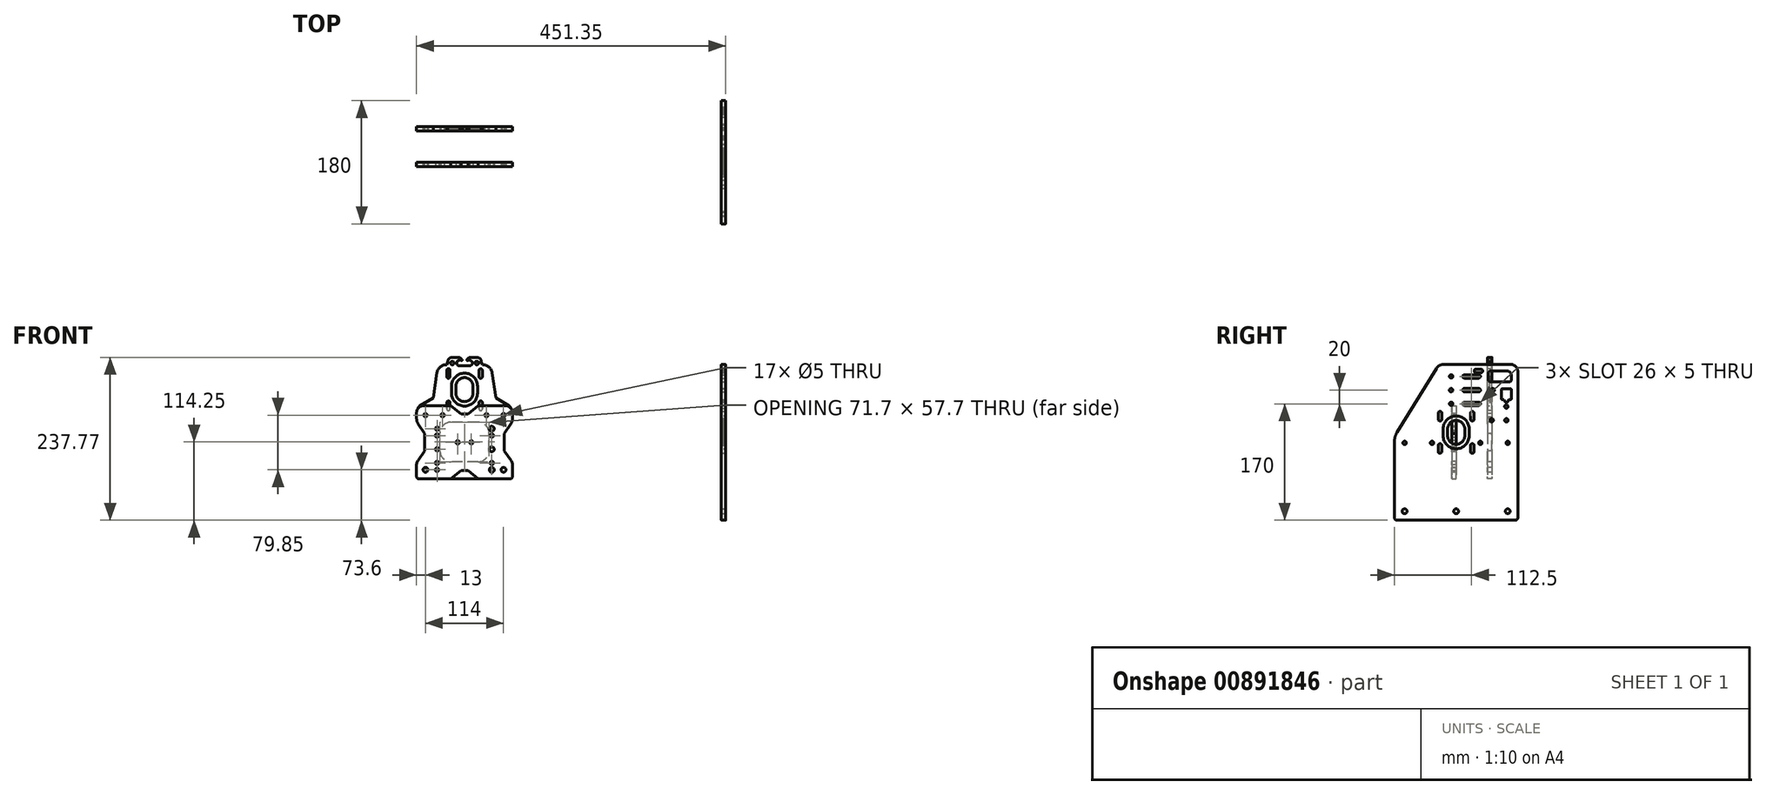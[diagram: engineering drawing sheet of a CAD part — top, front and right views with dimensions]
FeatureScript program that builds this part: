
annotation { "Feature Type Name" : "Feature", "Feature Type Description" : "" }
export const myFeature = defineFeature(function(context is Context, id is Id, definition is map)
    precondition{}
    {
        {
            var Q0;
            Q0=qCreatedBy(makeId("Right.planeOp"),FACE);
            var sketch = newSketch(context, id + "F0", { "sketchPlane" : qUnion([Q0])});
            skLineSegment(sketch, "E0", {"start": v(-28.77, 108.05) * mm, "end": v(-86.28, 14.78) * mm});
            skLineSegment(sketch, "E1", {"start": v(-90, 1.66) * mm, "end": v(-90, -110.25) * mm});
            skLineSegment(sketch, "E2", {"start": v(-86.5, -113.75) * mm, "end": v(86.5, -113.75) * mm});
            skLineSegment(sketch, "E3", {"start": v(90, -110.25) * mm, "end": v(90, 103.75) * mm});
            skLineSegment(sketch, "E4", {"start": v(80, 113.75) * mm, "end": v(-18.55, 113.75) * mm});
            skLineSegment(sketch, "E5", {"start": v(0, -113.75) * mm, "end": v(0, 0) * mm, "construction": true});
            skLineSegment(sketch, "E6", {"start": v(0, 0) * mm, "end": v(0, 113.75) * mm, "construction": true});
            skPoint(sketch, "E7.visualSharp", {"position": v(-25.25, 113.75) * mm});
            skArc(sketch, "E7.filletArc", {"start": v(-18.55, 113.75) * mm, "mid": v(-24.4, 112.23) * mm, "end": v(-28.77, 108.05) * mm});
            skPoint(sketch, "E8.visualSharp", {"position": v(90, 113.75) * mm});
            skArc(sketch, "E8.filletArc", {"start": v(90, 103.75) * mm, "mid": v(87.07, 110.82) * mm, "end": v(80, 113.75) * mm});
            skPoint(sketch, "E9.visualSharp", {"position": v(-90, -113.75) * mm});
            skArc(sketch, "E9.filletArc", {"start": v(-90, -110.25) * mm, "mid": v(-88.97, -112.72) * mm, "end": v(-86.5, -113.75) * mm});
            skPoint(sketch, "E10.visualSharp", {"position": v(90, -113.75) * mm});
            skArc(sketch, "E10.filletArc", {"start": v(86.5, -113.75) * mm, "mid": v(88.97, -112.72) * mm, "end": v(90, -110.25) * mm});
            skPoint(sketch, "E11.visualSharp", {"position": v(-90, 8.75) * mm});
            skArc(sketch, "E11.filletArc", {"start": v(-86.28, 14.78) * mm, "mid": v(-89.05, 8.48) * mm, "end": v(-90, 1.66) * mm});
            skSolve(sketch);
        }
        {
            var Q0;
            Q0=qSketchRegion(id+"F0",true);
            extrude(context, id + "F1", {"entities" : qUnion([Q0]), "depth" : 6.35 * mm});
        }
        {
            var Q0;
            Q0=makeQuery(id+"F1.opExtrude","CAP_FACE",FACE,{"disambiguationData":[OSD([sQuery(id+"F0.wireOp",EDGE,"E0"),sQuery(id+"F0.wireOp",EDGE,"E1"),sQuery(id+"F0.wireOp",EDGE,"E2"),sQuery(id+"F0.wireOp",EDGE,"E3"),sQuery(id+"F0.wireOp",EDGE,"E4"),sQuery(id+"F0.wireOp",EDGE,"E7.filletArc"),sQuery(id+"F0.wireOp",EDGE,"E8.filletArc"),sQuery(id+"F0.wireOp",EDGE,"E9.filletArc"),sQuery(id+"F0.wireOp",EDGE,"E10.filletArc"),sQuery(id+"F0.wireOp",EDGE,"E11.filletArc")])],"isStart":false});
            var sketch = newSketch(context, id + "F2", { "sketchPlane" : qUnion([Q0])});
            skLineSegment(sketch, "E12", {"start": v(0, 0) * mm, "end": v(0, -100.75) * mm, "construction": true});
            skLineSegment(sketch, "E13", {"start": v(0, -100.75) * mm, "end": v(75.3, -100.75) * mm, "construction": true});
            skLineSegment(sketch, "E14", {"start": v(0, -100.75) * mm, "end": v(-75.3, -100.75) * mm, "construction": true});
            skCircle(sketch, "E15", {"center": v(-75.3, -100.75) * mm, "radius": 3.57 * mm});
            skCircle(sketch, "E16", {"center": v(75.3, -100.75) * mm, "radius": 3.57 * mm});
            skCircle(sketch, "E17", {"center": v(0, -100.75) * mm, "radius": 3.57 * mm});
            skLineSegment(sketch, "E18", {"start": v(-75.3, -0.75) * mm, "end": v(-35.3, -0.75) * mm, "construction": true});
            skLineSegment(sketch, "E19", {"start": v(-35.3, -0.75) * mm, "end": v(0, -0.75) * mm, "construction": true});
            skLineSegment(sketch, "E20", {"start": v(0, -0.75) * mm, "end": v(35.3, -0.75) * mm, "construction": true});
            skLineSegment(sketch, "E21", {"start": v(35.3, -0.75) * mm, "end": v(75.3, -0.75) * mm, "construction": true});
            skCircle(sketch, "E22", {"center": v(-75.3, -0.75) * mm, "radius": 2.5 * mm});
            skCircle(sketch, "E23", {"center": v(-35.3, -0.75) * mm, "radius": 2.5 * mm});
            skCircle(sketch, "E24", {"center": v(35.3, -0.75) * mm, "radius": 2.5 * mm});
            skCircle(sketch, "E25", {"center": v(75.3, -0.75) * mm, "radius": 2.5 * mm});
            skLineSegment(sketch, "E26", {"start": v(-75.3, -0.75) * mm, "end": v(-75.3, -100.75) * mm, "construction": true});
            skLineSegment(sketch, "E27", {"start": v(75.3, -0.75) * mm, "end": v(75.3, -100.75) * mm, "construction": true});
            skSolve(sketch);
        }
        {
            var Q0;
            Q0=qSketchRegion(id+"F2",true);
            extrude(context, id + "F3", {"entities" : qUnion([Q0]), "operationType" : NewBodyOperationType.REMOVE, "endBound" : BoundingType.THROUGH_ALL, "oppositeDirection" : true, "depth" : 25 * mm});
        }
        {
            var Q0;
            Q0=makeQuery(id+"F1.opExtrude","CAP_FACE",FACE,{"disambiguationData":[OSD([sQuery(id+"F0.wireOp",EDGE,"E0"),sQuery(id+"F0.wireOp",EDGE,"E1"),sQuery(id+"F0.wireOp",EDGE,"E2"),sQuery(id+"F0.wireOp",EDGE,"E3"),sQuery(id+"F0.wireOp",EDGE,"E4"),sQuery(id+"F0.wireOp",EDGE,"E7.filletArc"),sQuery(id+"F0.wireOp",EDGE,"E8.filletArc"),sQuery(id+"F0.wireOp",EDGE,"E9.filletArc"),sQuery(id+"F0.wireOp",EDGE,"E10.filletArc"),sQuery(id+"F0.wireOp",EDGE,"E11.filletArc")])],"isStart":false});
            var sketch = newSketch(context, id + "F4", { "sketchPlane" : qUnion([Q0])});
            skArc(sketch, "E28", {"start": v(-12.5, 9.55) * mm, "mid": v(0, -2.95) * mm, "end": v(12.5, 9.55) * mm});
            skLineSegment(sketch, "E29", {"start": v(-12.5, 9.55) * mm, "end": v(-12.5, 19.55) * mm});
            skLineSegment(sketch, "E30", {"start": v(12.5, 19.55) * mm, "end": v(12.5, 9.55) * mm});
            skArc(sketch, "E31", {"start": v(-12.5, 19.55) * mm, "mid": v(0, 32.05) * mm, "end": v(12.5, 19.55) * mm});
            skLineSegment(sketch, "E32", {"start": v(0, 19.55) * mm, "end": v(0, 9.55) * mm, "construction": true});
            skLineSegment(sketch, "E33", {"start": v(-35.3, -0.75) * mm, "end": v(35.3, -0.75) * mm, "construction": true});
            skLineSegment(sketch, "E34", {"start": v(-23.57, 42.62) * mm, "end": v(-23.57, 33.62) * mm, "construction": true});
            skArc(sketch, "E35", {"start": v(-21.02, 42.62) * mm, "mid": v(-23.57, 45.17) * mm, "end": v(-26.12, 42.62) * mm});
            skArc(sketch, "E36", {"start": v(-26.12, 33.62) * mm, "mid": v(-23.57, 31.07) * mm, "end": v(-21.02, 33.62) * mm});
            skLineSegment(sketch, "E37", {"start": v(-21.02, 42.62) * mm, "end": v(-21.02, 33.62) * mm});
            skLineSegment(sketch, "E38", {"start": v(-26.12, 33.62) * mm, "end": v(-26.12, 42.62) * mm});
            skLineSegment(sketch, "E39", {"start": v(-12.5, 14.55) * mm, "end": v(12.5, 14.55) * mm, "construction": true});
            skLineSegment(sketch, "E40.MirrorCS", {"start": v(23.57, 42.62) * mm, "end": v(23.57, 33.62) * mm, "construction": true});
            skArc(sketch, "E41.MirrorCS", {"start": v(26.12, 33.62) * mm, "mid": v(23.57, 31.07) * mm, "end": v(21.02, 33.62) * mm});
            skLineSegment(sketch, "E42.MirrorCS", {"start": v(21.02, 42.62) * mm, "end": v(21.02, 33.62) * mm});
            skArc(sketch, "E43.MirrorCS", {"start": v(21.02, 42.62) * mm, "mid": v(23.57, 45.17) * mm, "end": v(26.12, 42.62) * mm});
            skLineSegment(sketch, "E44.MirrorCS", {"start": v(26.12, 33.62) * mm, "end": v(26.12, 42.62) * mm});
            skArc(sketch, "E45.MirrorCS", {"start": v(26.12, -4.52) * mm, "mid": v(23.57, -1.97) * mm, "end": v(21.02, -4.52) * mm});
            skLineSegment(sketch, "E46.MirrorCS", {"start": v(26.12, -4.52) * mm, "end": v(26.12, -13.52) * mm});
            skLineSegment(sketch, "E47.MirrorCS", {"start": v(-23.57, -13.52) * mm, "end": v(-23.57, -4.52) * mm, "construction": true});
            skLineSegment(sketch, "E48.MirrorCS", {"start": v(23.57, -13.52) * mm, "end": v(23.57, -4.52) * mm, "construction": true});
            skArc(sketch, "E49.MirrorCS", {"start": v(21.02, -13.52) * mm, "mid": v(23.57, -16.07) * mm, "end": v(26.12, -13.52) * mm});
            skLineSegment(sketch, "E50.MirrorCS", {"start": v(21.02, -13.52) * mm, "end": v(21.02, -4.52) * mm});
            skArc(sketch, "E51.MirrorCS", {"start": v(-26.12, -4.52) * mm, "mid": v(-23.57, -1.97) * mm, "end": v(-21.02, -4.52) * mm});
            skLineSegment(sketch, "E52.MirrorCS", {"start": v(-21.02, -13.52) * mm, "end": v(-21.02, -4.52) * mm});
            skArc(sketch, "E53.MirrorCS", {"start": v(-21.02, -13.52) * mm, "mid": v(-23.57, -16.07) * mm, "end": v(-26.12, -13.52) * mm});
            skLineSegment(sketch, "E54.MirrorCS", {"start": v(-26.12, -4.52) * mm, "end": v(-26.12, -13.52) * mm});
            skLineSegment(sketch, "E55", {"start": v(-23.57, 38.12) * mm, "end": v(23.57, -9.02) * mm, "construction": true});
            skLineSegment(sketch, "E56", {"start": v(23.57, -9.02) * mm, "end": v(-23.57, -9.02) * mm, "construction": true});
            skLineSegment(sketch, "E57", {"start": v(-23.57, -9.02) * mm, "end": v(23.57, 38.12) * mm, "construction": true});
            skSolve(sketch);
        }
        {
            var Q0;
            Q0=qSketchRegion(id+"F4",true);
            extrude(context, id + "F5", {"entities" : qUnion([Q0]), "operationType" : NewBodyOperationType.REMOVE, "endBound" : BoundingType.THROUGH_ALL, "oppositeDirection" : true, "depth" : 25 * mm});
        }
        {
            var Q0;
            Q0=makeQuery(id+"F1.opExtrude","CAP_FACE",FACE,{"disambiguationData":[OSD([sQuery(id+"F0.wireOp",EDGE,"E0"),sQuery(id+"F0.wireOp",EDGE,"E1"),sQuery(id+"F0.wireOp",EDGE,"E2"),sQuery(id+"F0.wireOp",EDGE,"E3"),sQuery(id+"F0.wireOp",EDGE,"E4"),sQuery(id+"F0.wireOp",EDGE,"E7.filletArc"),sQuery(id+"F0.wireOp",EDGE,"E8.filletArc"),sQuery(id+"F0.wireOp",EDGE,"E9.filletArc"),sQuery(id+"F0.wireOp",EDGE,"E10.filletArc"),sQuery(id+"F0.wireOp",EDGE,"E11.filletArc")])],"isStart":false});
            var sketch = newSketch(context, id + "F6", { "sketchPlane" : qUnion([Q0])});
            skCircle(sketch, "E58", {"center": v(-7.35, 96.25) * mm, "radius": 2.5 * mm});
            skLineSegment(sketch, "E59", {"start": v(-7.35, 96.25) * mm, "end": v(12, 96.25) * mm, "construction": true});
            skLineSegment(sketch, "E60", {"start": v(12, 96.25) * mm, "end": v(33, 96.25) * mm, "construction": true});
            skArc(sketch, "E61", {"start": v(12, 93.75) * mm, "mid": v(9.5, 96.25) * mm, "end": v(12, 98.75) * mm});
            skArc(sketch, "E62", {"start": v(33, 98.75) * mm, "mid": v(35.5, 96.25) * mm, "end": v(33, 93.75) * mm});
            skLineSegment(sketch, "E63", {"start": v(12, 98.75) * mm, "end": v(33, 98.75) * mm});
            skLineSegment(sketch, "E64", {"start": v(12, 93.75) * mm, "end": v(33, 93.75) * mm});
            skCircle(sketch, "E65.0.1.0", {"center": v(-7.35, 76.25) * mm, "radius": 2.5 * mm});
            skLineSegment(sketch, "E65.0.1.1", {"start": v(-7.35, 76.25) * mm, "end": v(12, 76.25) * mm, "construction": true});
            skArc(sketch, "E65.0.1.2", {"start": v(12, 73.75) * mm, "mid": v(9.5, 76.25) * mm, "end": v(12, 78.75) * mm});
            skLineSegment(sketch, "E65.0.1.3", {"start": v(12, 78.75) * mm, "end": v(33, 78.75) * mm});
            skLineSegment(sketch, "E65.0.1.4", {"start": v(12, 73.75) * mm, "end": v(33, 73.75) * mm});
            skArc(sketch, "E65.0.1.5", {"start": v(33, 78.75) * mm, "mid": v(35.5, 76.25) * mm, "end": v(33, 73.75) * mm});
            skCircle(sketch, "E65.0.2.0", {"center": v(-7.35, 56.25) * mm, "radius": 2.5 * mm});
            skLineSegment(sketch, "E65.0.2.1", {"start": v(-7.35, 56.25) * mm, "end": v(12, 56.25) * mm, "construction": true});
            skArc(sketch, "E65.0.2.2", {"start": v(12, 53.75) * mm, "mid": v(9.5, 56.25) * mm, "end": v(12, 58.75) * mm});
            skLineSegment(sketch, "E65.0.2.3", {"start": v(12, 58.75) * mm, "end": v(33, 58.75) * mm});
            skLineSegment(sketch, "E65.0.2.4", {"start": v(12, 53.75) * mm, "end": v(33, 53.75) * mm});
            skArc(sketch, "E65.0.2.5", {"start": v(33, 58.75) * mm, "mid": v(35.5, 56.25) * mm, "end": v(33, 53.75) * mm});
            skLineSegment(sketch, "E65.direction1", {"start": v(-7.35, 96.25) * mm, "end": v(-7.35, 96.25) * mm});
            skLineSegment(sketch, "E65.direction2", {"start": v(-7.35, 96.25) * mm, "end": v(-7.35, 76.25) * mm, "construction": true});
            skLineSegment(sketch, "E66", {"start": v(33, 76.25) * mm, "end": v(12, 76.25) * mm, "construction": true});
            skLineSegment(sketch, "E67", {"start": v(12, 56.25) * mm, "end": v(33, 56.25) * mm, "construction": true});
            skLineSegment(sketch, "E68", {"start": v(33, 76.25) * mm, "end": v(53.35, 76.25) * mm, "construction": true});
            skPoint(sketch, "E68.endSnap0", {"position": v(35.5, 76.25) * mm});
            skCircle(sketch, "E69", {"center": v(53.35, 76.25) * mm, "radius": 2.5 * mm});
            skSolve(sketch);
        }
        {
            var Q0;
            Q0=qSketchRegion(id+"F6",true);
            extrude(context, id + "F7", {"entities" : qUnion([Q0]), "operationType" : NewBodyOperationType.REMOVE, "endBound" : BoundingType.THROUGH_ALL, "oppositeDirection" : true, "depth" : 25 * mm});
        }
        {
            var Q0;
            Q0=makeQuery(id+"F1.opExtrude","CAP_FACE",FACE,{"disambiguationData":[OSD([sQuery(id+"F0.wireOp",EDGE,"E0"),sQuery(id+"F0.wireOp",EDGE,"E1"),sQuery(id+"F0.wireOp",EDGE,"E2"),sQuery(id+"F0.wireOp",EDGE,"E3"),sQuery(id+"F0.wireOp",EDGE,"E4"),sQuery(id+"F0.wireOp",EDGE,"E7.filletArc"),sQuery(id+"F0.wireOp",EDGE,"E8.filletArc"),sQuery(id+"F0.wireOp",EDGE,"E9.filletArc"),sQuery(id+"F0.wireOp",EDGE,"E10.filletArc"),sQuery(id+"F0.wireOp",EDGE,"E11.filletArc")])],"isStart":false});
            var sketch = newSketch(context, id + "F8", { "sketchPlane" : qUnion([Q0])});
            skLineSegment(sketch, "E70", {"start": v(12, 96.25) * mm, "end": v(33, 96.25) * mm, "construction": true});
            skLineSegment(sketch, "E71.bottom", {"start": v(28.1, 106.75) * mm, "end": v(36.9, 106.75) * mm});
            skLineSegment(sketch, "E71.top", {"start": v(28.1, 101.75) * mm, "end": v(36.9, 101.75) * mm});
            skLineSegment(sketch, "E71.left", {"start": v(26.5, 105.15) * mm, "end": v(26.5, 103.35) * mm});
            skLineSegment(sketch, "E71.right", {"start": v(38.5, 105.15) * mm, "end": v(38.5, 103.35) * mm});
            skPoint(sketch, "E72.visualSharp", {"position": v(26.5, 101.75) * mm});
            skArc(sketch, "E72.filletArc", {"start": v(26.5, 103.35) * mm, "mid": v(26.97, 102.22) * mm, "end": v(28.1, 101.75) * mm});
            skPoint(sketch, "E73.visualSharp", {"position": v(26.5, 106.75) * mm});
            skArc(sketch, "E73.filletArc", {"start": v(28.1, 106.75) * mm, "mid": v(26.97, 106.28) * mm, "end": v(26.5, 105.15) * mm});
            skPoint(sketch, "E74.visualSharp", {"position": v(38.5, 106.75) * mm});
            skArc(sketch, "E74.filletArc", {"start": v(38.5, 105.15) * mm, "mid": v(38.03, 106.28) * mm, "end": v(36.9, 106.75) * mm});
            skPoint(sketch, "E75.visualSharp", {"position": v(38.5, 101.75) * mm});
            skArc(sketch, "E75.filletArc", {"start": v(36.9, 101.75) * mm, "mid": v(38.03, 102.22) * mm, "end": v(38.5, 103.35) * mm});
            skLineSegment(sketch, "E76", {"start": v(26.5, 104.25) * mm, "end": v(38.5, 104.25) * mm, "construction": true});
            skLineSegment(sketch, "E77", {"start": v(32.5, 106.75) * mm, "end": v(32.5, 101.75) * mm, "construction": true});
            skLineSegment(sketch, "E78", {"start": v(22.5, 96.25) * mm, "end": v(22.5, 56.25) * mm, "construction": true});
            skPoint(sketch, "E78.endSnap0", {"position": v(22.5, 58.75) * mm});
            skLineSegment(sketch, "E79", {"start": v(12, 56.25) * mm, "end": v(33, 56.25) * mm, "construction": true});
            skSolve(sketch);
        }
        {
            var Q0;
            Q0=qSketchRegion(id+"F8",true);
            extrude(context, id + "F9", {"entities" : qUnion([Q0]), "operationType" : NewBodyOperationType.REMOVE, "endBound" : BoundingType.THROUGH_ALL, "oppositeDirection" : true, "depth" : 25 * mm});
        }
        {
            var Q0;
            Q0=makeQuery(id+"F1.opExtrude","CAP_FACE",FACE,{"disambiguationData":[OSD([sQuery(id+"F0.wireOp",EDGE,"E0"),sQuery(id+"F0.wireOp",EDGE,"E1"),sQuery(id+"F0.wireOp",EDGE,"E2"),sQuery(id+"F0.wireOp",EDGE,"E3"),sQuery(id+"F0.wireOp",EDGE,"E4"),sQuery(id+"F0.wireOp",EDGE,"E7.filletArc"),sQuery(id+"F0.wireOp",EDGE,"E8.filletArc"),sQuery(id+"F0.wireOp",EDGE,"E9.filletArc"),sQuery(id+"F0.wireOp",EDGE,"E10.filletArc"),sQuery(id+"F0.wireOp",EDGE,"E11.filletArc")])],"isStart":false});
            var sketch = newSketch(context, id + "F10", { "sketchPlane" : qUnion([Q0])});
            skCircle(sketch, "E80", {"center": v(73.3, 52.25) * mm, "radius": 2.5 * mm});
            skLineSegment(sketch, "E81", {"start": v(73.3, 52.25) * mm, "end": v(73.3, 32.25) * mm, "construction": true});
            skCircle(sketch, "E82", {"center": v(73.3, 32.25) * mm, "radius": 2.5 * mm});
            skLineSegment(sketch, "E83", {"start": v(73.3, 32.25) * mm, "end": v(51.95, 32.25) * mm, "construction": true});
            skCircle(sketch, "E84", {"center": v(51.95, 32.25) * mm, "radius": 2.5 * mm});
            skLineSegment(sketch, "E85", {"start": v(12, 56.25) * mm, "end": v(33, 56.25) * mm, "construction": true});
            skLineSegment(sketch, "E86", {"start": v(33, 56.25) * mm, "end": v(33, 52.25) * mm, "construction": true});
            skLineSegment(sketch, "E87", {"start": v(33, 52.25) * mm, "end": v(73.3, 52.25) * mm, "construction": true});
            skSolve(sketch);
        }
        {
            var Q0;
            Q0=qSketchRegion(id+"F10",true);
            extrude(context, id + "F11", {"entities" : qUnion([Q0]), "operationType" : NewBodyOperationType.REMOVE, "endBound" : BoundingType.THROUGH_ALL, "oppositeDirection" : true, "depth" : 25 * mm});
        }
        {
            var Q0;
            Q0=makeQuery(id+"F1.opExtrude","CAP_FACE",FACE,{"disambiguationData":[OSD([sQuery(id+"F0.wireOp",EDGE,"E0"),sQuery(id+"F0.wireOp",EDGE,"E1"),sQuery(id+"F0.wireOp",EDGE,"E2"),sQuery(id+"F0.wireOp",EDGE,"E3"),sQuery(id+"F0.wireOp",EDGE,"E4"),sQuery(id+"F0.wireOp",EDGE,"E7.filletArc"),sQuery(id+"F0.wireOp",EDGE,"E8.filletArc"),sQuery(id+"F0.wireOp",EDGE,"E9.filletArc"),sQuery(id+"F0.wireOp",EDGE,"E10.filletArc"),sQuery(id+"F0.wireOp",EDGE,"E11.filletArc")])],"isStart":false});
            var sketch = newSketch(context, id + "F12", { "sketchPlane" : qUnion([Q0])});
            skLineSegment(sketch, "E88", {"start": v(65.95, 76.8) * mm, "end": v(65.95, 63.85) * mm});
            skLineSegment(sketch, "E89", {"start": v(67.55, 62.25) * mm, "end": v(69.65, 62.25) * mm});
            skLineSegment(sketch, "E90", {"start": v(69.65, 62.25) * mm, "end": v(70.8, 60.75) * mm});
            skLineSegment(sketch, "E91", {"start": v(75.8, 60.75) * mm, "end": v(76.95, 62.25) * mm});
            skLineSegment(sketch, "E92", {"start": v(76.95, 62.25) * mm, "end": v(79.05, 62.25) * mm});
            skLineSegment(sketch, "E93", {"start": v(80.65, 63.85) * mm, "end": v(80.65, 76.8) * mm});
            skLineSegment(sketch, "E94", {"start": v(79.05, 78.4) * mm, "end": v(67.55, 78.4) * mm});
            skArc(sketch, "E95", {"start": v(70.8, 60.75) * mm, "mid": v(73.3, 58.25) * mm, "end": v(75.8, 60.75) * mm});
            skLineSegment(sketch, "E96", {"start": v(73.3, 60.75) * mm, "end": v(73.3, 52.25) * mm, "construction": true});
            skLineSegment(sketch, "E97", {"start": v(73.3, 78.4) * mm, "end": v(73.3, 60.75) * mm, "construction": true});
            skLineSegment(sketch, "E98", {"start": v(65.95, 70.32) * mm, "end": v(80.65, 70.32) * mm, "construction": true});
            skPoint(sketch, "E99.visualSharp", {"position": v(65.95, 62.25) * mm});
            skArc(sketch, "E99.filletArc", {"start": v(65.95, 63.85) * mm, "mid": v(66.42, 62.72) * mm, "end": v(67.55, 62.25) * mm});
            skPoint(sketch, "E100.visualSharp", {"position": v(65.95, 78.4) * mm});
            skArc(sketch, "E100.filletArc", {"start": v(67.55, 78.4) * mm, "mid": v(66.42, 77.93) * mm, "end": v(65.95, 76.8) * mm});
            skPoint(sketch, "E101.visualSharp", {"position": v(80.65, 78.4) * mm});
            skArc(sketch, "E101.filletArc", {"start": v(80.65, 76.8) * mm, "mid": v(80.18, 77.93) * mm, "end": v(79.05, 78.4) * mm});
            skPoint(sketch, "E102.visualSharp", {"position": v(80.65, 62.25) * mm});
            skArc(sketch, "E102.filletArc", {"start": v(79.05, 62.25) * mm, "mid": v(80.18, 62.72) * mm, "end": v(80.65, 63.85) * mm});
            skLineSegment(sketch, "E103", {"start": v(80.65, 91.4) * mm, "end": v(80.65, 97.6) * mm});
            skLineSegment(sketch, "E104", {"start": v(74, 104.25) * mm, "end": v(50.3, 104.25) * mm});
            skLineSegment(sketch, "E105", {"start": v(47.15, 101.1) * mm, "end": v(47.15, 91.4) * mm});
            skLineSegment(sketch, "E106", {"start": v(50.3, 88.25) * mm, "end": v(77.5, 88.25) * mm});
            skPoint(sketch, "E107.visualSharp", {"position": v(80.65, 104.25) * mm});
            skArc(sketch, "E107.filletArc", {"start": v(80.65, 97.6) * mm, "mid": v(78.7, 102.3) * mm, "end": v(74, 104.25) * mm});
            skPoint(sketch, "E108.visualSharp", {"position": v(80.65, 88.25) * mm});
            skArc(sketch, "E108.filletArc", {"start": v(77.5, 88.25) * mm, "mid": v(79.73, 89.17) * mm, "end": v(80.65, 91.4) * mm});
            skPoint(sketch, "E109.visualSharp", {"position": v(47.15, 88.25) * mm});
            skArc(sketch, "E109.filletArc", {"start": v(47.15, 91.4) * mm, "mid": v(48.07, 89.17) * mm, "end": v(50.3, 88.25) * mm});
            skPoint(sketch, "E110.visualSharp", {"position": v(47.15, 104.25) * mm});
            skArc(sketch, "E110.filletArc", {"start": v(50.3, 104.25) * mm, "mid": v(48.07, 103.33) * mm, "end": v(47.15, 101.1) * mm});
            skSolve(sketch);
        }
        {
            var Q0;
            Q0=qSketchRegion(id+"F12",true);
            extrude(context, id + "F13", {"entities" : qUnion([Q0]), "operationType" : NewBodyOperationType.REMOVE, "endBound" : BoundingType.THROUGH_ALL, "oppositeDirection" : true, "depth" : 25 * mm});
        }
        {
            var Q0;
            Q0=makeQuery(id+"F1.opExtrude","SWEPT_BODY",BODY,{"disambiguationData":[OSD([sQuery(id+"F0.wireOp",EDGE,"E0"),sQuery(id+"F0.wireOp",EDGE,"E1"),sQuery(id+"F0.wireOp",EDGE,"E2"),sQuery(id+"F0.wireOp",EDGE,"E3"),sQuery(id+"F0.wireOp",EDGE,"E4"),sQuery(id+"F0.wireOp",EDGE,"E7.filletArc"),sQuery(id+"F0.wireOp",EDGE,"E8.filletArc"),sQuery(id+"F0.wireOp",EDGE,"E9.filletArc"),sQuery(id+"F0.wireOp",EDGE,"E10.filletArc"),sQuery(id+"F0.wireOp",EDGE,"E11.filletArc")])]});
            transform(context, id + "F14", {"entities" : qUnion([Q0]), "transformType" : TransformType.TRANSLATION_3D, "dx" : (750 / 2) * mm, "dy" : 0 * mm, "dz" : 0 * mm, "makeCopy" : false});
        }
        {
            var Q0;
            Q0=qCreatedBy(makeId("Front.planeOp"),FACE);
            var sketch = newSketch(context, id + "F15", { "sketchPlane" : qUnion([Q0])});
            skLineSegment(sketch, "E111", {"start": v(0, 0) * mm, "end": v(0, 41.2) * mm, "construction": true});
            skLineSegment(sketch, "E112", {"start": v(0, 0) * mm, "end": v(0, -41.2) * mm, "construction": true});
            skLineSegment(sketch, "E113", {"start": v(0, 41.2) * mm, "end": v(5, 41.2) * mm});
            skLineSegment(sketch, "E114", {"start": v(20, 53.35) * mm, "end": v(5, 41.2) * mm});
            skLineSegment(sketch, "E115", {"start": v(20, 53.35) * mm, "end": v(70, 53.35) * mm});
            skLineSegment(sketch, "E116", {"start": v(70, 53.35) * mm, "end": v(70, 30.5) * mm});
            skLineSegment(sketch, "E117", {"start": v(70, 30.5) * mm, "end": v(58, 12.75) * mm});
            skLineSegment(sketch, "E118", {"start": v(58, 12.75) * mm, "end": v(58, -12.75) * mm});
            skLineSegment(sketch, "E119", {"start": v(58, -12.75) * mm, "end": v(70, -29.25) * mm});
            skLineSegment(sketch, "E120", {"start": v(70, -29.25) * mm, "end": v(70, -53.35) * mm});
            skLineSegment(sketch, "E121", {"start": v(70, -53.35) * mm, "end": v(20, -53.35) * mm});
            skLineSegment(sketch, "E122", {"start": v(20, -53.35) * mm, "end": v(5, -41.2) * mm});
            skLineSegment(sketch, "E123", {"start": v(5, -41.2) * mm, "end": v(0, -41.2) * mm});
            skLineSegment(sketch, "E124", {"start": v(20, 53.35) * mm, "end": v(20, -53.35) * mm, "construction": true});
            skLineSegment(sketch, "E125", {"start": v(0, 41.2) * mm, "end": v(0, 53.35) * mm, "construction": true});
            skLineSegment(sketch, "E126", {"start": v(0, 53.35) * mm, "end": v(20, 53.35) * mm, "construction": true});
            skLineSegment(sketch, "E127", {"start": v(0, -41.2) * mm, "end": v(0, -53.35) * mm, "construction": true});
            skLineSegment(sketch, "E128", {"start": v(0, -53.35) * mm, "end": v(20, -53.35) * mm, "construction": true});
            skLineSegment(sketch, "E129", {"start": v(5, 41.2) * mm, "end": v(5, -41.2) * mm, "construction": true});
            skLineSegment(sketch, "E130", {"start": v(0, 0) * mm, "end": v(58, 0) * mm, "construction": true});
            skLineSegment(sketch, "E131", {"start": v(70, 30.5) * mm, "end": v(70, -29.25) * mm, "construction": true});
            skLineSegment(sketch, "E132.MirrorCS", {"start": v(-5, -41.2) * mm, "end": v(0, -41.2) * mm});
            skLineSegment(sketch, "E133.MirrorCS", {"start": v(-20, -53.35) * mm, "end": v(-5, -41.2) * mm});
            skLineSegment(sketch, "E134.MirrorCS", {"start": v(-70, -53.35) * mm, "end": v(-20, -53.35) * mm});
            skLineSegment(sketch, "E135.MirrorCS", {"start": v(-70, -29.25) * mm, "end": v(-70, -53.35) * mm});
            skLineSegment(sketch, "E136.MirrorCS", {"start": v(-58, -12.75) * mm, "end": v(-70, -29.25) * mm});
            skLineSegment(sketch, "E137.MirrorCS", {"start": v(-58, 12.75) * mm, "end": v(-58, -12.75) * mm});
            skLineSegment(sketch, "E138.MirrorCS", {"start": v(-70, 30.5) * mm, "end": v(-58, 12.75) * mm});
            skLineSegment(sketch, "E139.MirrorCS", {"start": v(-70, 53.35) * mm, "end": v(-70, 30.5) * mm});
            skLineSegment(sketch, "E140.MirrorCS", {"start": v(-20, 53.35) * mm, "end": v(-70, 53.35) * mm});
            skLineSegment(sketch, "E141.MirrorCS", {"start": v(0, 41.2) * mm, "end": v(-5, 41.2) * mm});
            skLineSegment(sketch, "E142.MirrorCS", {"start": v(-20, 53.35) * mm, "end": v(-5, 41.2) * mm});
            skSolve(sketch);
        }
        {
            var Q0;
            Q0=qSketchRegion(id+"F15",true);
            extrude(context, id + "F16", {"entities" : qUnion([Q0]), "depth" : 6.35 * mm});
        }
        {
            var Q0;
            Q0=makeQuery(id+"F16.opExtrude","CAP_FACE",FACE,{"disambiguationData":[OSD([sQuery(id+"F15.wireOp",EDGE,"E113"),sQuery(id+"F15.wireOp",EDGE,"E114"),sQuery(id+"F15.wireOp",EDGE,"E115"),sQuery(id+"F15.wireOp",EDGE,"E116"),sQuery(id+"F15.wireOp",EDGE,"E117"),sQuery(id+"F15.wireOp",EDGE,"E118"),sQuery(id+"F15.wireOp",EDGE,"E119"),sQuery(id+"F15.wireOp",EDGE,"E120"),sQuery(id+"F15.wireOp",EDGE,"E121"),sQuery(id+"F15.wireOp",EDGE,"E122"),sQuery(id+"F15.wireOp",EDGE,"E123"),sQuery(id+"F15.wireOp",EDGE,"E132.MirrorCS"),sQuery(id+"F15.wireOp",EDGE,"E133.MirrorCS"),sQuery(id+"F15.wireOp",EDGE,"E134.MirrorCS"),sQuery(id+"F15.wireOp",EDGE,"E135.MirrorCS"),sQuery(id+"F15.wireOp",EDGE,"E136.MirrorCS"),sQuery(id+"F15.wireOp",EDGE,"E137.MirrorCS"),sQuery(id+"F15.wireOp",EDGE,"E138.MirrorCS"),sQuery(id+"F15.wireOp",EDGE,"E139.MirrorCS"),sQuery(id+"F15.wireOp",EDGE,"E140.MirrorCS"),sQuery(id+"F15.wireOp",EDGE,"E141.MirrorCS"),sQuery(id+"F15.wireOp",EDGE,"E142.MirrorCS")])],"isStart":false});
            var sketch = newSketch(context, id + "F17", { "sketchPlane" : qUnion([Q0])});
            skLineSegment(sketch, "E143", {"start": v(0, 0) * mm, "end": v(10, 0) * mm, "construction": true});
            skLineSegment(sketch, "E144", {"start": v(0, 0) * mm, "end": v(-10, 0) * mm, "construction": true});
            skCircle(sketch, "E145", {"center": v(-10, 0) * mm, "radius": 2.5 * mm});
            skCircle(sketch, "E146", {"center": v(10, 0) * mm, "radius": 2.5 * mm});
            skSolve(sketch);
        }
        {
            var Q0;
            Q0=qSketchRegion(id+"F17",true);
            extrude(context, id + "F18", {"entities" : qUnion([Q0]), "operationType" : NewBodyOperationType.REMOVE, "endBound" : BoundingType.THROUGH_ALL, "oppositeDirection" : true, "depth" : 25 * mm});
        }
        {
            var Q0;
            Q0=makeQuery(id+"F16.opExtrude","CAP_FACE",FACE,{"disambiguationData":[OSD([sQuery(id+"F15.wireOp",EDGE,"E113"),sQuery(id+"F15.wireOp",EDGE,"E114"),sQuery(id+"F15.wireOp",EDGE,"E115"),sQuery(id+"F15.wireOp",EDGE,"E116"),sQuery(id+"F15.wireOp",EDGE,"E117"),sQuery(id+"F15.wireOp",EDGE,"E118"),sQuery(id+"F15.wireOp",EDGE,"E119"),sQuery(id+"F15.wireOp",EDGE,"E120"),sQuery(id+"F15.wireOp",EDGE,"E121"),sQuery(id+"F15.wireOp",EDGE,"E122"),sQuery(id+"F15.wireOp",EDGE,"E123"),sQuery(id+"F15.wireOp",EDGE,"E132.MirrorCS"),sQuery(id+"F15.wireOp",EDGE,"E133.MirrorCS"),sQuery(id+"F15.wireOp",EDGE,"E134.MirrorCS"),sQuery(id+"F15.wireOp",EDGE,"E135.MirrorCS"),sQuery(id+"F15.wireOp",EDGE,"E136.MirrorCS"),sQuery(id+"F15.wireOp",EDGE,"E137.MirrorCS"),sQuery(id+"F15.wireOp",EDGE,"E138.MirrorCS"),sQuery(id+"F15.wireOp",EDGE,"E139.MirrorCS"),sQuery(id+"F15.wireOp",EDGE,"E140.MirrorCS"),sQuery(id+"F15.wireOp",EDGE,"E141.MirrorCS"),sQuery(id+"F15.wireOp",EDGE,"E142.MirrorCS")])],"isStart":false});
            var sketch = newSketch(context, id + "F19", { "sketchPlane" : qUnion([Q0])});
            skLineSegment(sketch, "E147", {"start": v(0, 41.2) * mm, "end": v(0, -41.2) * mm, "construction": true});
            skLineSegment(sketch, "E148", {"start": v(32, 39.7) * mm, "end": v(57, 39.7) * mm, "construction": true});
            skCircle(sketch, "E149", {"center": v(32, 39.7) * mm, "radius": 2.5 * mm});
            skCircle(sketch, "E150", {"center": v(57, 39.7) * mm, "radius": 2.5 * mm});
            skCircle(sketch, "E151", {"center": v(57, -40.1) * mm, "radius": 3.57 * mm});
            skCircle(sketch, "E152.MirrorC", {"center": v(-57, -40.1) * mm, "radius": 3.57 * mm});
            skCircle(sketch, "E153.MirrorC", {"center": v(-57, 39.7) * mm, "radius": 2.5 * mm});
            skCircle(sketch, "E154.MirrorC", {"center": v(-32, 39.7) * mm, "radius": 2.5 * mm});
            skLineSegment(sketch, "E155", {"start": v(-57, 39.7) * mm, "end": v(-32, 39.7) * mm, "construction": true});
            skLineSegment(sketch, "E156", {"start": v(57, 39.7) * mm, "end": v(57, -40.1) * mm, "construction": true});
            skLineSegment(sketch, "E157", {"start": v(-57, 39.7) * mm, "end": v(-57, -40.1) * mm, "construction": true});
            skLineSegment(sketch, "E158", {"start": v(-57, -40.1) * mm, "end": v(57, -40.1) * mm, "construction": true});
            skLineSegment(sketch, "E159", {"start": v(-32, 39.7) * mm, "end": v(32, 39.7) * mm, "construction": true});
            skSolve(sketch);
        }
        {
            var Q0;
            Q0=qSketchRegion(id+"F19",true);
            extrude(context, id + "F20", {"entities" : qUnion([Q0]), "operationType" : NewBodyOperationType.REMOVE, "endBound" : BoundingType.THROUGH_ALL, "oppositeDirection" : true, "depth" : 25 * mm});
        }
        {
            var Q0;
            Q0=makeQuery(id+"F16.opExtrude","CAP_FACE",FACE,{"disambiguationData":[OSD([sQuery(id+"F15.wireOp",EDGE,"E113"),sQuery(id+"F15.wireOp",EDGE,"E114"),sQuery(id+"F15.wireOp",EDGE,"E115"),sQuery(id+"F15.wireOp",EDGE,"E116"),sQuery(id+"F15.wireOp",EDGE,"E117"),sQuery(id+"F15.wireOp",EDGE,"E118"),sQuery(id+"F15.wireOp",EDGE,"E119"),sQuery(id+"F15.wireOp",EDGE,"E120"),sQuery(id+"F15.wireOp",EDGE,"E121"),sQuery(id+"F15.wireOp",EDGE,"E122"),sQuery(id+"F15.wireOp",EDGE,"E123"),sQuery(id+"F15.wireOp",EDGE,"E132.MirrorCS"),sQuery(id+"F15.wireOp",EDGE,"E133.MirrorCS"),sQuery(id+"F15.wireOp",EDGE,"E134.MirrorCS"),sQuery(id+"F15.wireOp",EDGE,"E135.MirrorCS"),sQuery(id+"F15.wireOp",EDGE,"E136.MirrorCS"),sQuery(id+"F15.wireOp",EDGE,"E137.MirrorCS"),sQuery(id+"F15.wireOp",EDGE,"E138.MirrorCS"),sQuery(id+"F15.wireOp",EDGE,"E139.MirrorCS"),sQuery(id+"F15.wireOp",EDGE,"E140.MirrorCS"),sQuery(id+"F15.wireOp",EDGE,"E141.MirrorCS"),sQuery(id+"F15.wireOp",EDGE,"E142.MirrorCS")])],"isStart":false});
            var sketch = newSketch(context, id + "F21", { "sketchPlane" : qUnion([Q0])});
            skLineSegment(sketch, "E160", {"start": v(0, 41.2) * mm, "end": v(0, -41.2) * mm, "construction": true});
            skLineSegment(sketch, "E161", {"start": v(39.8, 9.85) * mm, "end": v(39.8, -10.15) * mm, "construction": true});
            skLineSegment(sketch, "E162", {"start": v(39.8, -10.15) * mm, "end": v(39.8, -30.15) * mm, "construction": true});
            skLineSegment(sketch, "E163", {"start": v(39.8, 9.85) * mm, "end": v(39.8, 19.85) * mm, "construction": true});
            skLineSegment(sketch, "E164", {"start": v(39.8, -30.15) * mm, "end": v(39.8, -40.15) * mm, "construction": true});
            skCircle(sketch, "E165", {"center": v(39.8, 19.85) * mm, "radius": 3.57 * mm});
            skCircle(sketch, "E166", {"center": v(39.8, -10.15) * mm, "radius": 3.57 * mm});
            skCircle(sketch, "E167", {"center": v(39.8, -40.15) * mm, "radius": 3.57 * mm});
            skCircle(sketch, "E168", {"center": v(39.8, 9.85) * mm, "radius": 2.5 * mm});
            skCircle(sketch, "E169", {"center": v(39.8, -30.15) * mm, "radius": 2.5 * mm});
            skLineSegment(sketch, "E170", {"start": v(39.8, -10.15) * mm, "end": v(0, -10.15) * mm, "construction": true});
            skLineSegment(sketch, "E171", {"start": v(-40, 9.85) * mm, "end": v(-40, 19.85) * mm, "construction": true});
            skLineSegment(sketch, "E172", {"start": v(-40, -30.15) * mm, "end": v(-40, -40.15) * mm, "construction": true});
            skCircle(sketch, "E173", {"center": v(-40, 19.85) * mm, "radius": 2.5 * mm});
            skCircle(sketch, "E174", {"center": v(-40, 9.85) * mm, "radius": 2.5 * mm});
            skCircle(sketch, "E175", {"center": v(-40, -10.15) * mm, "radius": 2.5 * mm});
            skCircle(sketch, "E176", {"center": v(-40, -30.15) * mm, "radius": 2.5 * mm});
            skCircle(sketch, "E177", {"center": v(-40, -40.15) * mm, "radius": 2.5 * mm});
            skLineSegment(sketch, "E178", {"start": v(-40, -30.15) * mm, "end": v(-40, -10.15) * mm, "construction": true});
            skLineSegment(sketch, "E179", {"start": v(-40, 9.85) * mm, "end": v(-40, -10.15) * mm, "construction": true});
            skLineSegment(sketch, "E180", {"start": v(-40, -10.15) * mm, "end": v(0, -10.15) * mm, "construction": true});
            skSolve(sketch);
        }
        {
            var Q0;
            Q0=qSketchRegion(id+"F21",true);
            extrude(context, id + "F22", {"entities" : qUnion([Q0]), "operationType" : NewBodyOperationType.REMOVE, "endBound" : BoundingType.THROUGH_ALL, "oppositeDirection" : true, "depth" : 25 * mm});
        }
        {
            var Q0;
            Q0=makeQuery(id+"F16.opExtrude","SWEPT_EDGE",EDGE,{"disambiguationData":[OSD([sQuery(id+"F15.wireOp",EDGE,"E139.MirrorCS"),sQuery(id+"F15.wireOp",EDGE,"E140.MirrorCS")])]});
            var Q1;
            Q1=makeQuery(id+"F16.opExtrude","SWEPT_EDGE",EDGE,{"disambiguationData":[OSD([sQuery(id+"F15.wireOp",EDGE,"E115"),sQuery(id+"F15.wireOp",EDGE,"E116")])]});
            fillet(context, id + "F23", {"entities" : qUnion([Q0, Q1]), "radius" : 9.6 * mm, "tangentPropagation" : true, "allowEdgeOverflow" : false});
        }
        {
            var Q0;
            Q0=makeQuery(id+"F16.opExtrude","SWEPT_EDGE",EDGE,{"disambiguationData":[OSD([sQuery(id+"F15.wireOp",EDGE,"E120"),sQuery(id+"F15.wireOp",EDGE,"E121")])]});
            var Q1;
            Q1=makeQuery(id+"F16.opExtrude","SWEPT_EDGE",EDGE,{"disambiguationData":[OSD([sQuery(id+"F15.wireOp",EDGE,"E134.MirrorCS"),sQuery(id+"F15.wireOp",EDGE,"E135.MirrorCS")])]});
            fillet(context, id + "F24", {"entities" : qUnion([Q0, Q1]), "radius" : 3.36 * mm, "tangentPropagation" : true, "allowEdgeOverflow" : false});
        }
        {
            var Q0;
            Q0=makeQuery(id+"F16.opExtrude","SWEPT_EDGE",EDGE,{"disambiguationData":[OSD([sQuery(id+"F15.wireOp",EDGE,"E116"),sQuery(id+"F15.wireOp",EDGE,"E117")])]});
            var Q1;
            Q1=makeQuery(id+"F16.opExtrude","SWEPT_EDGE",EDGE,{"disambiguationData":[OSD([sQuery(id+"F15.wireOp",EDGE,"E138.MirrorCS"),sQuery(id+"F15.wireOp",EDGE,"E139.MirrorCS")])]});
            fillet(context, id + "F25", {"entities" : qUnion([Q0, Q1]), "radius" : 14 * mm, "tangentPropagation" : true, "allowEdgeOverflow" : false});
        }
        {
            var Q0;
            Q0=makeQuery(id+"F16.opExtrude","SWEPT_EDGE",EDGE,{"disambiguationData":[OSD([sQuery(id+"F15.wireOp",EDGE,"E119"),sQuery(id+"F15.wireOp",EDGE,"E120")])]});
            var Q1;
            Q1=makeQuery(id+"F16.opExtrude","SWEPT_EDGE",EDGE,{"disambiguationData":[OSD([sQuery(id+"F15.wireOp",EDGE,"E135.MirrorCS"),sQuery(id+"F15.wireOp",EDGE,"E136.MirrorCS")])]});
            fillet(context, id + "F26", {"entities" : qUnion([Q0, Q1]), "radius" : 11 * mm, "tangentPropagation" : true, "allowEdgeOverflow" : false});
        }
        {
            var Q0;
            Q0=makeQuery(id+"F16.opExtrude","CAP_FACE",FACE,{"disambiguationData":[OSD([sQuery(id+"F15.wireOp",EDGE,"E113"),sQuery(id+"F15.wireOp",EDGE,"E114"),sQuery(id+"F15.wireOp",EDGE,"E115"),sQuery(id+"F15.wireOp",EDGE,"E116"),sQuery(id+"F15.wireOp",EDGE,"E117"),sQuery(id+"F15.wireOp",EDGE,"E118"),sQuery(id+"F15.wireOp",EDGE,"E119"),sQuery(id+"F15.wireOp",EDGE,"E120"),sQuery(id+"F15.wireOp",EDGE,"E121"),sQuery(id+"F15.wireOp",EDGE,"E122"),sQuery(id+"F15.wireOp",EDGE,"E123"),sQuery(id+"F15.wireOp",EDGE,"E132.MirrorCS"),sQuery(id+"F15.wireOp",EDGE,"E133.MirrorCS"),sQuery(id+"F15.wireOp",EDGE,"E134.MirrorCS"),sQuery(id+"F15.wireOp",EDGE,"E135.MirrorCS"),sQuery(id+"F15.wireOp",EDGE,"E136.MirrorCS"),sQuery(id+"F15.wireOp",EDGE,"E137.MirrorCS"),sQuery(id+"F15.wireOp",EDGE,"E138.MirrorCS"),sQuery(id+"F15.wireOp",EDGE,"E139.MirrorCS"),sQuery(id+"F15.wireOp",EDGE,"E140.MirrorCS"),sQuery(id+"F15.wireOp",EDGE,"E141.MirrorCS"),sQuery(id+"F15.wireOp",EDGE,"E142.MirrorCS")])],"isStart":true});
            cPlane(context, id + "F27", {"entities" : qUnion([Q0]), "cplaneType" : CPlaneType.OFFSET, "offset" : 46 * mm, "width" : 150 * mm, "height" : 150 * mm});
        }
        {
            var Q0;
            Q0=qCreatedBy(id+"F27.planeOp",FACE);
            var sketch = newSketch(context, id + "F28", { "sketchPlane" : qUnion([Q0])});
            skLineSegment(sketch, "E181", {"start": v(0, 0) * mm, "end": v(0, -53.35) * mm, "construction": true});
            skLineSegment(sketch, "E182", {"start": v(-67.5, 51.95) * mm, "end": v(-45.84, 64.81) * mm});
            skLineSegment(sketch, "E183", {"start": v(-45.84, 64.81) * mm, "end": v(-38.5, 113.35) * mm});
            skLineSegment(sketch, "E184", {"start": v(-38.5, 113.35) * mm, "end": v(-26, 113.35) * mm});
            skLineSegment(sketch, "E185", {"start": v(-26, 113.35) * mm, "end": v(-22.45, 124.02) * mm, "construction": true});
            skLineSegment(sketch, "E186", {"start": v(-22.45, 124.02) * mm, "end": v(0, 124.02) * mm, "construction": true});
            skLineSegment(sketch, "E187", {"start": v(0, 124.02) * mm, "end": v(0, 0) * mm, "construction": true});
            skLineSegment(sketch, "E188.MirrorCS", {"start": v(22.45, 124.02) * mm, "end": v(0, 124.02) * mm, "construction": true});
            skLineSegment(sketch, "E189.MirrorCS", {"start": v(26, 113.35) * mm, "end": v(22.45, 124.02) * mm, "construction": true});
            skLineSegment(sketch, "E190.MirrorCS", {"start": v(38.5, 113.35) * mm, "end": v(26, 113.35) * mm});
            skLineSegment(sketch, "E191.MirrorCS", {"start": v(45.84, 64.81) * mm, "end": v(38.5, 113.35) * mm});
            skLineSegment(sketch, "E192.MirrorCS", {"start": v(67.5, 51.95) * mm, "end": v(45.84, 64.81) * mm});
            skLineSegment(sketch, "E193", {"start": v(45.84, 64.81) * mm, "end": v(45.84, 113.35) * mm, "construction": true});
            skArc(sketch, "E194.0", {"start": v(70, 34.79) * mm, "mid": v(69.39, 30.69) * mm, "end": v(67.6, 26.95) * mm});
            skLineSegment(sketch, "E195.0", {"start": v(67.6, 26.95) * mm, "end": v(58, 12.75) * mm});
            skLineSegment(sketch, "E196.0", {"start": v(58, 12.75) * mm, "end": v(58, -12.75) * mm});
            skLineSegment(sketch, "E197.0", {"start": v(58, -12.75) * mm, "end": v(67.9, -26.36) * mm});
            skArc(sketch, "E198.0", {"start": v(67.9, -26.36) * mm, "mid": v(69.46, -29.43) * mm, "end": v(70, -32.83) * mm});
            skLineSegment(sketch, "E199.0", {"start": v(70, -32.83) * mm, "end": v(70, -49.99) * mm});
            skArc(sketch, "E200.0", {"start": v(70, -49.99) * mm, "mid": v(69.02, -52.37) * mm, "end": v(66.64, -53.35) * mm});
            skLineSegment(sketch, "E201.0", {"start": v(66.64, -53.35) * mm, "end": v(20, -53.35) * mm});
            skLineSegment(sketch, "E202.0", {"start": v(-66.64, -53.35) * mm, "end": v(-20, -53.35) * mm});
            skArc(sketch, "E203.0", {"start": v(-66.64, -53.35) * mm, "mid": v(-69.02, -52.37) * mm, "end": v(-70, -49.99) * mm});
            skLineSegment(sketch, "E204.0", {"start": v(-70, -32.83) * mm, "end": v(-70, -49.99) * mm});
            skArc(sketch, "E205.0", {"start": v(-70, -32.83) * mm, "mid": v(-69.46, -29.43) * mm, "end": v(-67.9, -26.36) * mm});
            skLineSegment(sketch, "E206.0", {"start": v(-58, -12.75) * mm, "end": v(-67.9, -26.36) * mm});
            skLineSegment(sketch, "E207.0", {"start": v(-58, 12.75) * mm, "end": v(-58, -12.75) * mm});
            skLineSegment(sketch, "E208.0", {"start": v(-67.6, 26.95) * mm, "end": v(-58, 12.75) * mm});
            skArc(sketch, "E209.0", {"start": v(-70, 34.79) * mm, "mid": v(-69.39, 30.69) * mm, "end": v(-67.6, 26.95) * mm});
            skLineSegment(sketch, "E210", {"start": v(70, 34.79) * mm, "end": v(67.5, 51.95) * mm});
            skLineSegment(sketch, "E211", {"start": v(-67.5, 51.95) * mm, "end": v(-70, 34.79) * mm});
            skLineSegment(sketch, "E212", {"start": v(20, -53.35) * mm, "end": v(-20, -53.35) * mm});
            skLineSegment(sketch, "E213", {"start": v(-67.5, 51.95) * mm, "end": v(-67.5, 104.82) * mm, "construction": true});
            skLineSegment(sketch, "E214", {"start": v(24.5, 117.85) * mm, "end": v(-24.5, 117.85) * mm, "construction": true});
            skLineSegment(sketch, "E215", {"start": v(26, 113.35) * mm, "end": v(24.5, 117.85) * mm});
            skLineSegment(sketch, "E216", {"start": v(-24.5, 117.85) * mm, "end": v(-26, 113.35) * mm});
            skArc(sketch, "E217", {"start": v(24.5, 117.85) * mm, "mid": v(22.7, 122.21) * mm, "end": v(18.33, 124.02) * mm});
            skArc(sketch, "E218.MirrorCS", {"start": v(-24.5, 117.85) * mm, "mid": v(-22.7, 122.21) * mm, "end": v(-18.33, 124.02) * mm});
            skLineSegment(sketch, "E219", {"start": v(18.33, 124.02) * mm, "end": v(-18.33, 124.02) * mm});
            skSolve(sketch);
        }
        {
            var Q0;
            Q0=qSketchRegion(id+"F28",true);
            extrude(context, id + "F29", {"entities" : qUnion([Q0]), "depth" : 6.35 * mm});
        }
        {
            var Q0;
            Q0=makeQuery(id+"F29.opExtrude","CAP_FACE",FACE,{"disambiguationData":[OSD([sQuery(id+"F28.wireOp",EDGE,"Hsz0tEu8-2u2z-894v-u5uz-qeEPLO7T1y3h"),sQuery(id+"F28.wireOp",EDGE,"vEOOrqZs-7KoW-orxh-Vkwo-SEQycOVZhe9Y"),sQuery(id+"F28.wireOp",EDGE,"aVo1oUrC-5gOD-S3Gd-KdpA-WAxqIndI85XZ"),sQuery(id+"F28.wireOp",EDGE,"9HF069ls-R4vM-rCiR-Mglt-uF1vui31pR4p"),sQuery(id+"F28.wireOp",EDGE,"6UwIWVSN-CBoj-eV2b-T7fp-u49lRc933uwu"),sQuery(id+"F28.wireOp",EDGE,"xATdj4HU-5i3P-5F5E-4dWz-QLdLokjUGgyJ"),sQuery(id+"F28.wireOp",EDGE,"E182"),sQuery(id+"F28.wireOp",EDGE,"E183"),sQuery(id+"F28.wireOp",EDGE,"E184"),sQuery(id+"F28.wireOp",EDGE,"E185"),sQuery(id+"F28.wireOp",EDGE,"E186"),sQuery(id+"F28.wireOp",EDGE,"01ed5a7f-363f-42f9-805d-97d743e7f8c00.MirrorCS"),sQuery(id+"F28.wireOp",EDGE,"E188.MirrorCS"),sQuery(id+"F28.wireOp",EDGE,"E189.MirrorCS"),sQuery(id+"F28.wireOp",EDGE,"E190.MirrorCS"),sQuery(id+"F28.wireOp",EDGE,"E191.MirrorCS"),sQuery(id+"F28.wireOp",EDGE,"E192.MirrorCS"),sQuery(id+"F28.wireOp",EDGE,"01ed5a7f-363f-42f9-805d-97d743e7f8c06.MirrorCS"),sQuery(id+"F28.wireOp",EDGE,"01ed5a7f-363f-42f9-805d-97d743e7f8c08.MirrorCS"),sQuery(id+"F28.wireOp",EDGE,"01ed5a7f-363f-42f9-805d-97d743e7f8c09.MirrorCS"),sQuery(id+"F28.wireOp",EDGE,"orUJIb6K-YDtt-LamK-tEY8-xfgMmjDqjYYe"),sQuery(id+"F28.wireOp",EDGE,"c8cb6b1b-2073-4661-974d-9f2328fd6722"),sQuery(id+"F28.wireOp",EDGE,"7cc86124-f559-48ea-aabb-f436df0639fe0.MirrorCS"),sQuery(id+"F28.wireOp",EDGE,"7cc86124-f559-48ea-aabb-f436df0639fe1.MirrorCS")])],"isStart":true});
            var sketch = newSketch(context, id + "F30", { "sketchPlane" : qUnion([Q0])});
            skCircle(sketch, "E220.0", {"center": v(-57, 39.7) * mm, "radius": 2.5 * mm});
            skCircle(sketch, "E221.0", {"center": v(-32, 39.7) * mm, "radius": 2.5 * mm});
            skCircle(sketch, "E222.0", {"center": v(32, 39.7) * mm, "radius": 2.5 * mm});
            skCircle(sketch, "E223.0", {"center": v(57, 39.7) * mm, "radius": 2.5 * mm});
            skCircle(sketch, "E224.0", {"center": v(-57, -40.1) * mm, "radius": 3.57 * mm});
            skCircle(sketch, "E225.0", {"center": v(57, -40.1) * mm, "radius": 3.57 * mm});
            skSolve(sketch);
        }
        {
            var Q0;
            Q0=qSketchRegion(id+"F30",true);
            extrude(context, id + "F31", {"entities" : qUnion([Q0]), "operationType" : NewBodyOperationType.REMOVE, "endBound" : BoundingType.THROUGH_ALL, "oppositeDirection" : true, "depth" : 25 * mm});
        }
        {
            var Q0;
            Q0=makeQuery(id+"F29.opExtrude","SWEPT_EDGE",EDGE,{"disambiguationData":[OSD([sQuery(id+"F28.wireOp",EDGE,"E183"),sQuery(id+"F28.wireOp",EDGE,"E184")])]});
            var Q1;
            Q1=makeQuery(id+"F29.opExtrude","SWEPT_EDGE",EDGE,{"disambiguationData":[OSD([sQuery(id+"F28.wireOp",EDGE,"E190.MirrorCS"),sQuery(id+"F28.wireOp",EDGE,"E191.MirrorCS")])]});
            fillet(context, id + "F32", {"entities" : qUnion([Q0, Q1]), "radius" : 13.7 * mm, "tangentPropagation" : true, "allowEdgeOverflow" : false});
        }
        {
            var Q0;
            Q0=makeQuery(id+"F29.opExtrude","SWEPT_EDGE",EDGE,{"disambiguationData":[OSD([sQuery(id+"F28.wireOp",EDGE,"E182"),sQuery(id+"F28.wireOp",EDGE,"E211")])]});
            var Q1;
            Q1=makeQuery(id+"F29.opExtrude","SWEPT_EDGE",EDGE,{"disambiguationData":[OSD([sQuery(id+"F28.wireOp",EDGE,"E192.MirrorCS"),sQuery(id+"F28.wireOp",EDGE,"E210")])]});
            fillet(context, id + "F33", {"entities" : qUnion([Q0, Q1]), "radius" : 5.5 * mm, "tangentPropagation" : true, "allowEdgeOverflow" : false});
        }
        {
            var Q0;
            Q0=makeQuery(id+"F29.opExtrude","CAP_FACE",FACE,{"disambiguationData":[OSD([sQuery(id+"F28.wireOp",EDGE,"E182"),sQuery(id+"F28.wireOp",EDGE,"E183"),sQuery(id+"F28.wireOp",EDGE,"E184"),sQuery(id+"F28.wireOp",EDGE,"E185"),sQuery(id+"F28.wireOp",EDGE,"E186"),sQuery(id+"F28.wireOp",EDGE,"E188.MirrorCS"),sQuery(id+"F28.wireOp",EDGE,"E189.MirrorCS"),sQuery(id+"F28.wireOp",EDGE,"E190.MirrorCS"),sQuery(id+"F28.wireOp",EDGE,"E191.MirrorCS"),sQuery(id+"F28.wireOp",EDGE,"E192.MirrorCS"),sQuery(id+"F28.wireOp",EDGE,"E194.0"),sQuery(id+"F28.wireOp",EDGE,"E195.0"),sQuery(id+"F28.wireOp",EDGE,"E196.0"),sQuery(id+"F28.wireOp",EDGE,"E197.0"),sQuery(id+"F28.wireOp",EDGE,"E198.0"),sQuery(id+"F28.wireOp",EDGE,"E199.0"),sQuery(id+"F28.wireOp",EDGE,"E200.0"),sQuery(id+"F28.wireOp",EDGE,"E201.0"),sQuery(id+"F28.wireOp",EDGE,"E202.0"),sQuery(id+"F28.wireOp",EDGE,"E203.0"),sQuery(id+"F28.wireOp",EDGE,"E204.0"),sQuery(id+"F28.wireOp",EDGE,"E205.0"),sQuery(id+"F28.wireOp",EDGE,"E206.0"),sQuery(id+"F28.wireOp",EDGE,"E207.0"),sQuery(id+"F28.wireOp",EDGE,"E208.0"),sQuery(id+"F28.wireOp",EDGE,"E209.0"),sQuery(id+"F28.wireOp",EDGE,"E210"),sQuery(id+"F28.wireOp",EDGE,"E211"),sQuery(id+"F28.wireOp",EDGE,"E212")])],"isStart":true});
            var sketch = newSketch(context, id + "F34", { "sketchPlane" : qUnion([Q0])});
            skLineSegment(sketch, "E226.bottom", {"start": v(-19.85, 29.35) * mm, "end": v(19.85, 29.35) * mm});
            skLineSegment(sketch, "E226.top", {"start": v(-19.85, -28.35) * mm, "end": v(19.85, -28.35) * mm});
            skLineSegment(sketch, "E226.left", {"start": v(-35.85, 13.35) * mm, "end": v(-35.85, -12.35) * mm});
            skLineSegment(sketch, "E226.right", {"start": v(35.85, 13.35) * mm, "end": v(35.85, -12.35) * mm});
            skLineSegment(sketch, "E227", {"start": v(0, 29.35) * mm, "end": v(0, 0) * mm, "construction": true});
            skLineSegment(sketch, "E228", {"start": v(0, 0) * mm, "end": v(0, -28.35) * mm, "construction": true});
            skPoint(sketch, "E229.visualSharp", {"position": v(-35.85, 29.35) * mm});
            skArc(sketch, "E229.filletArc", {"start": v(-19.85, 29.35) * mm, "mid": v(-31.16, 24.66) * mm, "end": v(-35.85, 13.35) * mm});
            skPoint(sketch, "E230.visualSharp", {"position": v(35.85, 29.35) * mm});
            skArc(sketch, "E230.filletArc", {"start": v(35.85, 13.35) * mm, "mid": v(31.16, 24.66) * mm, "end": v(19.85, 29.35) * mm});
            skPoint(sketch, "E231.visualSharp", {"position": v(35.85, -28.35) * mm});
            skArc(sketch, "E231.filletArc", {"start": v(19.85, -28.35) * mm, "mid": v(31.16, -23.66) * mm, "end": v(35.85, -12.35) * mm});
            skPoint(sketch, "E232.visualSharp", {"position": v(-35.85, -28.35) * mm});
            skArc(sketch, "E232.filletArc", {"start": v(-35.85, -12.35) * mm, "mid": v(-31.16, -23.66) * mm, "end": v(-19.85, -28.35) * mm});
            skSolve(sketch);
        }
        {
            var Q0;
            Q0=qSketchRegion(id+"F34",true);
            extrude(context, id + "F35", {"entities" : qUnion([Q0]), "operationType" : NewBodyOperationType.REMOVE, "endBound" : BoundingType.THROUGH_ALL, "oppositeDirection" : true, "depth" : 25 * mm});
        }
        {
            var Q0;
            Q0=makeQuery(id+"F29.opExtrude","CAP_FACE",FACE,{"disambiguationData":[OSD([sQuery(id+"F28.wireOp",EDGE,"E182"),sQuery(id+"F28.wireOp",EDGE,"E183"),sQuery(id+"F28.wireOp",EDGE,"E184"),sQuery(id+"F28.wireOp",EDGE,"E190.MirrorCS"),sQuery(id+"F28.wireOp",EDGE,"E191.MirrorCS"),sQuery(id+"F28.wireOp",EDGE,"E192.MirrorCS"),sQuery(id+"F28.wireOp",EDGE,"E194.0"),sQuery(id+"F28.wireOp",EDGE,"E195.0"),sQuery(id+"F28.wireOp",EDGE,"E196.0"),sQuery(id+"F28.wireOp",EDGE,"E197.0"),sQuery(id+"F28.wireOp",EDGE,"E198.0"),sQuery(id+"F28.wireOp",EDGE,"E199.0"),sQuery(id+"F28.wireOp",EDGE,"E200.0"),sQuery(id+"F28.wireOp",EDGE,"E201.0"),sQuery(id+"F28.wireOp",EDGE,"E202.0"),sQuery(id+"F28.wireOp",EDGE,"E203.0"),sQuery(id+"F28.wireOp",EDGE,"E204.0"),sQuery(id+"F28.wireOp",EDGE,"E205.0"),sQuery(id+"F28.wireOp",EDGE,"E206.0"),sQuery(id+"F28.wireOp",EDGE,"E207.0"),sQuery(id+"F28.wireOp",EDGE,"E208.0"),sQuery(id+"F28.wireOp",EDGE,"E209.0"),sQuery(id+"F28.wireOp",EDGE,"E210"),sQuery(id+"F28.wireOp",EDGE,"E211"),sQuery(id+"F28.wireOp",EDGE,"E212"),sQuery(id+"F28.wireOp",EDGE,"E215"),sQuery(id+"F28.wireOp",EDGE,"E216"),sQuery(id+"F28.wireOp",EDGE,"E217"),sQuery(id+"F28.wireOp",EDGE,"E218.MirrorCS"),sQuery(id+"F28.wireOp",EDGE,"E219")])],"isStart":true});
            var sketch = newSketch(context, id + "F36", { "sketchPlane" : qUnion([Q0])});
            skLineSegment(sketch, "E233", {"start": v(0, 29.35) * mm, "end": v(0, 124.02) * mm, "construction": true});
            skLineSegment(sketch, "E234", {"start": v(-3.5, 121.02) * mm, "end": v(-6.5, 124.02) * mm});
            skArc(sketch, "E235", {"start": v(-3.5, 121.02) * mm, "mid": v(-3.6, 119.52) * mm, "end": v(-5.08, 119.82) * mm});
            skLineSegment(sketch, "E236", {"start": v(-5.08, 119.82) * mm, "end": v(-7.5, 119.82) * mm});
            skArc(sketch, "E237", {"start": v(-7.5, 119.82) * mm, "mid": v(-11.5, 115.82) * mm, "end": v(-7.5, 111.82) * mm});
            skLineSegment(sketch, "E238", {"start": v(-7.5, 111.82) * mm, "end": v(0, 111.82) * mm});
            skLineSegment(sketch, "E239", {"start": v(-6.5, 124.02) * mm, "end": v(0, 124.02) * mm});
            skLineSegment(sketch, "E240.MirrorCS", {"start": v(7.5, 111.82) * mm, "end": v(0, 111.82) * mm});
            skArc(sketch, "E241.MirrorCS", {"start": v(7.5, 119.82) * mm, "mid": v(11.5, 115.82) * mm, "end": v(7.5, 111.82) * mm});
            skLineSegment(sketch, "E242.MirrorCS", {"start": v(5.08, 119.82) * mm, "end": v(7.5, 119.82) * mm});
            skArc(sketch, "E243.MirrorCS", {"start": v(3.5, 121.02) * mm, "mid": v(3.6, 119.52) * mm, "end": v(5.08, 119.82) * mm});
            skLineSegment(sketch, "E244.MirrorCS", {"start": v(3.5, 121.02) * mm, "end": v(6.5, 124.02) * mm});
            skLineSegment(sketch, "E245.MirrorCS", {"start": v(6.5, 124.02) * mm, "end": v(0, 124.02) * mm});
            skLineSegment(sketch, "E246", {"start": v(-7.5, 115.82) * mm, "end": v(-17.86, 115.82) * mm, "construction": true});
            skPoint(sketch, "E246.endSnap0", {"position": v(-11.5, 115.82) * mm});
            skCircle(sketch, "E247", {"center": v(-17.86, 115.82) * mm, "radius": 2.7 * mm});
            skLineSegment(sketch, "E248.MirrorCS", {"start": v(7.5, 115.82) * mm, "end": v(17.86, 115.82) * mm, "construction": true});
            skCircle(sketch, "E249.MirrorC", {"center": v(17.86, 115.82) * mm, "radius": 2.7 * mm});
            skSolve(sketch);
        }
        {
            var Q0;
            Q0=qSketchRegion(id+"F36",true);
            extrude(context, id + "F37", {"entities" : qUnion([Q0]), "operationType" : NewBodyOperationType.REMOVE, "endBound" : BoundingType.THROUGH_ALL, "oppositeDirection" : true, "depth" : 25 * mm});
        }
        {
            var Q0;
            Q0=makeQuery(id+"F29.opExtrude","CAP_FACE",FACE,{"disambiguationData":[OSD([sQuery(id+"F28.wireOp",EDGE,"E182"),sQuery(id+"F28.wireOp",EDGE,"E183"),sQuery(id+"F28.wireOp",EDGE,"E184"),sQuery(id+"F28.wireOp",EDGE,"E190.MirrorCS"),sQuery(id+"F28.wireOp",EDGE,"E191.MirrorCS"),sQuery(id+"F28.wireOp",EDGE,"E192.MirrorCS"),sQuery(id+"F28.wireOp",EDGE,"E194.0"),sQuery(id+"F28.wireOp",EDGE,"E195.0"),sQuery(id+"F28.wireOp",EDGE,"E196.0"),sQuery(id+"F28.wireOp",EDGE,"E197.0"),sQuery(id+"F28.wireOp",EDGE,"E198.0"),sQuery(id+"F28.wireOp",EDGE,"E199.0"),sQuery(id+"F28.wireOp",EDGE,"E200.0"),sQuery(id+"F28.wireOp",EDGE,"E201.0"),sQuery(id+"F28.wireOp",EDGE,"E202.0"),sQuery(id+"F28.wireOp",EDGE,"E203.0"),sQuery(id+"F28.wireOp",EDGE,"E204.0"),sQuery(id+"F28.wireOp",EDGE,"E205.0"),sQuery(id+"F28.wireOp",EDGE,"E206.0"),sQuery(id+"F28.wireOp",EDGE,"E207.0"),sQuery(id+"F28.wireOp",EDGE,"E208.0"),sQuery(id+"F28.wireOp",EDGE,"E209.0"),sQuery(id+"F28.wireOp",EDGE,"E210"),sQuery(id+"F28.wireOp",EDGE,"E211"),sQuery(id+"F28.wireOp",EDGE,"E212"),sQuery(id+"F28.wireOp",EDGE,"E215"),sQuery(id+"F28.wireOp",EDGE,"E216"),sQuery(id+"F28.wireOp",EDGE,"E217"),sQuery(id+"F28.wireOp",EDGE,"E218.MirrorCS"),sQuery(id+"F28.wireOp",EDGE,"E219")])],"isStart":true});
            var sketch = newSketch(context, id + "F38", { "sketchPlane" : qUnion([Q0])});
            skLineSegment(sketch, "E250", {"start": v(0, 0) * mm, "end": v(0, 71.97) * mm, "construction": true});
            skLineSegment(sketch, "E251", {"start": v(0, 71.97) * mm, "end": v(0, 81.97) * mm, "construction": true});
            skLineSegment(sketch, "E252", {"start": v(0, 81.97) * mm, "end": v(0, 111.82) * mm, "construction": true});
            skArc(sketch, "E253", {"start": v(-12.5, 81.97) * mm, "mid": v(0, 94.47) * mm, "end": v(12.5, 81.97) * mm});
            skArc(sketch, "E254", {"start": v(-12.5, 71.97) * mm, "mid": v(0, 59.47) * mm, "end": v(12.5, 71.97) * mm});
            skLineSegment(sketch, "E255", {"start": v(-12.5, 81.97) * mm, "end": v(-12.5, 71.97) * mm});
            skLineSegment(sketch, "E256", {"start": v(12.5, 81.97) * mm, "end": v(12.5, 71.97) * mm});
            skLineSegment(sketch, "E257", {"start": v(-23.57, 100.54) * mm, "end": v(0, 100.54) * mm, "construction": true});
            skLineSegment(sketch, "E258", {"start": v(0, 100.54) * mm, "end": v(23.57, 100.54) * mm, "construction": true});
            skLineSegment(sketch, "E259", {"start": v(23.57, 100.54) * mm, "end": v(0, 76.97) * mm, "construction": true});
            skLineSegment(sketch, "E260", {"start": v(0, 76.97) * mm, "end": v(-23.57, 53.4) * mm, "construction": true});
            skLineSegment(sketch, "E261", {"start": v(-23.57, 53.4) * mm, "end": v(0, 53.4) * mm, "construction": true});
            skLineSegment(sketch, "E262", {"start": v(0, 53.4) * mm, "end": v(23.57, 53.4) * mm, "construction": true});
            skLineSegment(sketch, "E263", {"start": v(23.57, 53.4) * mm, "end": v(0, 76.97) * mm, "construction": true});
            skLineSegment(sketch, "E264", {"start": v(0, 76.97) * mm, "end": v(-23.57, 100.54) * mm, "construction": true});
            skLineSegment(sketch, "E265", {"start": v(-23.57, 105.04) * mm, "end": v(-23.57, 96.04) * mm, "construction": true});
            skLineSegment(sketch, "E266", {"start": v(23.57, 105.04) * mm, "end": v(23.57, 96.04) * mm, "construction": true});
            skLineSegment(sketch, "E267", {"start": v(0, 76.97) * mm, "end": v(-12.5, 76.97) * mm, "construction": true});
            skLineSegment(sketch, "E268", {"start": v(-23.57, 57.9) * mm, "end": v(-23.57, 48.9) * mm, "construction": true});
            skLineSegment(sketch, "E269", {"start": v(23.57, 57.9) * mm, "end": v(23.57, 48.9) * mm, "construction": true});
            skArc(sketch, "E270", {"start": v(-26.07, 57.9) * mm, "mid": v(-23.57, 60.4) * mm, "end": v(-21.07, 57.9) * mm});
            skArc(sketch, "E271", {"start": v(-26.07, 48.9) * mm, "mid": v(-23.57, 46.4) * mm, "end": v(-21.07, 48.9) * mm});
            skLineSegment(sketch, "E272", {"start": v(-26.07, 57.9) * mm, "end": v(-26.07, 48.9) * mm});
            skLineSegment(sketch, "E273", {"start": v(-21.07, 57.9) * mm, "end": v(-21.07, 48.9) * mm});
            skArc(sketch, "E274.MirrorCS", {"start": v(26.07, 57.9) * mm, "mid": v(23.57, 60.4) * mm, "end": v(21.07, 57.9) * mm});
            skLineSegment(sketch, "E275.MirrorCS", {"start": v(26.07, 57.9) * mm, "end": v(26.07, 48.9) * mm});
            skLineSegment(sketch, "E276.MirrorCS", {"start": v(21.07, 57.9) * mm, "end": v(21.07, 48.9) * mm});
            skArc(sketch, "E277.MirrorCS", {"start": v(26.07, 48.9) * mm, "mid": v(23.57, 46.4) * mm, "end": v(21.07, 48.9) * mm});
            skLineSegment(sketch, "E278.MirrorCS", {"start": v(-26.07, 96.04) * mm, "end": v(-26.07, 105.04) * mm});
            skArc(sketch, "E279.MirrorCS", {"start": v(-26.07, 96.04) * mm, "mid": v(-23.57, 93.54) * mm, "end": v(-21.07, 96.04) * mm});
            skLineSegment(sketch, "E280.MirrorCS", {"start": v(-21.07, 96.04) * mm, "end": v(-21.07, 105.04) * mm});
            skArc(sketch, "E281.MirrorCS", {"start": v(-26.07, 105.04) * mm, "mid": v(-23.57, 107.54) * mm, "end": v(-21.07, 105.04) * mm});
            skArc(sketch, "E282.MirrorCS", {"start": v(26.07, 105.04) * mm, "mid": v(23.57, 107.54) * mm, "end": v(21.07, 105.04) * mm});
            skLineSegment(sketch, "E283.MirrorCS", {"start": v(21.07, 96.04) * mm, "end": v(21.07, 105.04) * mm});
            skArc(sketch, "E284.MirrorCS", {"start": v(26.07, 96.04) * mm, "mid": v(23.57, 93.54) * mm, "end": v(21.07, 96.04) * mm});
            skLineSegment(sketch, "E285.MirrorCS", {"start": v(26.07, 96.04) * mm, "end": v(26.07, 105.04) * mm});
            skSolve(sketch);
        }
        {
            var Q0;
            Q0=qSketchRegion(id+"F38",true);
            extrude(context, id + "F39", {"entities" : qUnion([Q0]), "operationType" : NewBodyOperationType.REMOVE, "endBound" : BoundingType.THROUGH_ALL, "oppositeDirection" : true, "depth" : 25 * mm});
        }
        {
            var Q0;
            Q0=makeQuery(id+"F1.opExtrude","CAP_FACE",FACE,{"disambiguationData":[OSD([sQuery(id+"F0.wireOp",EDGE,"E0"),sQuery(id+"F0.wireOp",EDGE,"E1"),sQuery(id+"F0.wireOp",EDGE,"E2"),sQuery(id+"F0.wireOp",EDGE,"E3"),sQuery(id+"F0.wireOp",EDGE,"E4"),sQuery(id+"F0.wireOp",EDGE,"E7.filletArc"),sQuery(id+"F0.wireOp",EDGE,"E8.filletArc"),sQuery(id+"F0.wireOp",EDGE,"E9.filletArc"),sQuery(id+"F0.wireOp",EDGE,"E10.filletArc"),sQuery(id+"F0.wireOp",EDGE,"E11.filletArc")])],"isStart":false});
            var sketch = newSketch(context, id + "F40", { "sketchPlane" : qUnion([Q0])});
            skArc(sketch, "E286", {"start": v(-19, 9.55) * mm, "mid": v(0, -9.45) * mm, "end": v(19, 9.55) * mm});
            skLineSegment(sketch, "E287.left", {"start": v(19, 9.55) * mm, "end": v(19, 19.55) * mm});
            skLineSegment(sketch, "E287.right", {"start": v(-19, 9.55) * mm, "end": v(-19, 19.55) * mm});
            skPoint(sketch, "E287.middle", {"position": v(0, 14.55) * mm});
            skPoint(sketch, "E287.middle.positionSnap0", {"position": v(-12.5, 14.55) * mm});
            skPoint(sketch, "E287.centerSnap0", {"position": v(-12.5, 14.55) * mm});
            skArc(sketch, "E288.trimOffspring", {"start": v(19, 19.55) * mm, "mid": v(0, 38.55) * mm, "end": v(-19, 19.55) * mm});
            skSolve(sketch);
        }
        {
            var Q0;
            Q0 = qSketchRegion(id + "F40", true);
            extrude(context, id + "F41", {"entities" : qUnion([Q0]), "operationType" : NewBodyOperationType.REMOVE, "oppositeDirection" : true, "depth" : 3 * mm, "offsetDistance" : 25 * mm});
        }
        {
            var Q0;
            Q0=makeQuery(id+"F29.opExtrude","CAP_FACE",FACE,{"disambiguationData":[OSD([sQuery(id+"F28.wireOp",EDGE,"E182"),sQuery(id+"F28.wireOp",EDGE,"E183"),sQuery(id+"F28.wireOp",EDGE,"E184"),sQuery(id+"F28.wireOp",EDGE,"E190.MirrorCS"),sQuery(id+"F28.wireOp",EDGE,"E191.MirrorCS"),sQuery(id+"F28.wireOp",EDGE,"E192.MirrorCS"),sQuery(id+"F28.wireOp",EDGE,"E194.0"),sQuery(id+"F28.wireOp",EDGE,"E195.0"),sQuery(id+"F28.wireOp",EDGE,"E196.0"),sQuery(id+"F28.wireOp",EDGE,"E197.0"),sQuery(id+"F28.wireOp",EDGE,"E198.0"),sQuery(id+"F28.wireOp",EDGE,"E199.0"),sQuery(id+"F28.wireOp",EDGE,"E200.0"),sQuery(id+"F28.wireOp",EDGE,"E201.0"),sQuery(id+"F28.wireOp",EDGE,"E202.0"),sQuery(id+"F28.wireOp",EDGE,"E203.0"),sQuery(id+"F28.wireOp",EDGE,"E204.0"),sQuery(id+"F28.wireOp",EDGE,"E205.0"),sQuery(id+"F28.wireOp",EDGE,"E206.0"),sQuery(id+"F28.wireOp",EDGE,"E207.0"),sQuery(id+"F28.wireOp",EDGE,"E208.0"),sQuery(id+"F28.wireOp",EDGE,"E209.0"),sQuery(id+"F28.wireOp",EDGE,"E210"),sQuery(id+"F28.wireOp",EDGE,"E211"),sQuery(id+"F28.wireOp",EDGE,"E212"),sQuery(id+"F28.wireOp",EDGE,"E215"),sQuery(id+"F28.wireOp",EDGE,"E216"),sQuery(id+"F28.wireOp",EDGE,"E217"),sQuery(id+"F28.wireOp",EDGE,"E218.MirrorCS"),sQuery(id+"F28.wireOp",EDGE,"E219")])],"isStart":true});
            var sketch = newSketch(context, id + "F42", { "sketchPlane" : qUnion([Q0])});
            skArc(sketch, "E289", {"start": v(19, 81.97) * mm, "mid": v(0, 100.97) * mm, "end": v(-19, 81.97) * mm});
            skArc(sketch, "E290", {"start": v(-19, 71.97) * mm, "mid": v(0, 52.97) * mm, "end": v(19, 71.97) * mm});
            skLineSegment(sketch, "E291.left", {"start": v(19, 71.97) * mm, "end": v(19, 81.97) * mm});
            skLineSegment(sketch, "E291.right", {"start": v(-19, 71.97) * mm, "end": v(-19, 81.97) * mm});
            skPoint(sketch, "E291.middle", {"position": v(0, 76.97) * mm});
            skPoint(sketch, "E291.middle.positionSnap0", {"position": v(-12.5, 76.97) * mm});
            skPoint(sketch, "E291.centerSnap0", {"position": v(-12.5, 76.97) * mm});
            skSolve(sketch);
        }
        {
            var Q0;
            Q0 = qSketchRegion(id + "F42", true);
            extrude(context, id + "F43", {"entities" : qUnion([Q0]), "operationType" : NewBodyOperationType.REMOVE, "oppositeDirection" : true, "depth" : 3 * mm, "offsetDistance" : 25 * mm});
        }
    });
